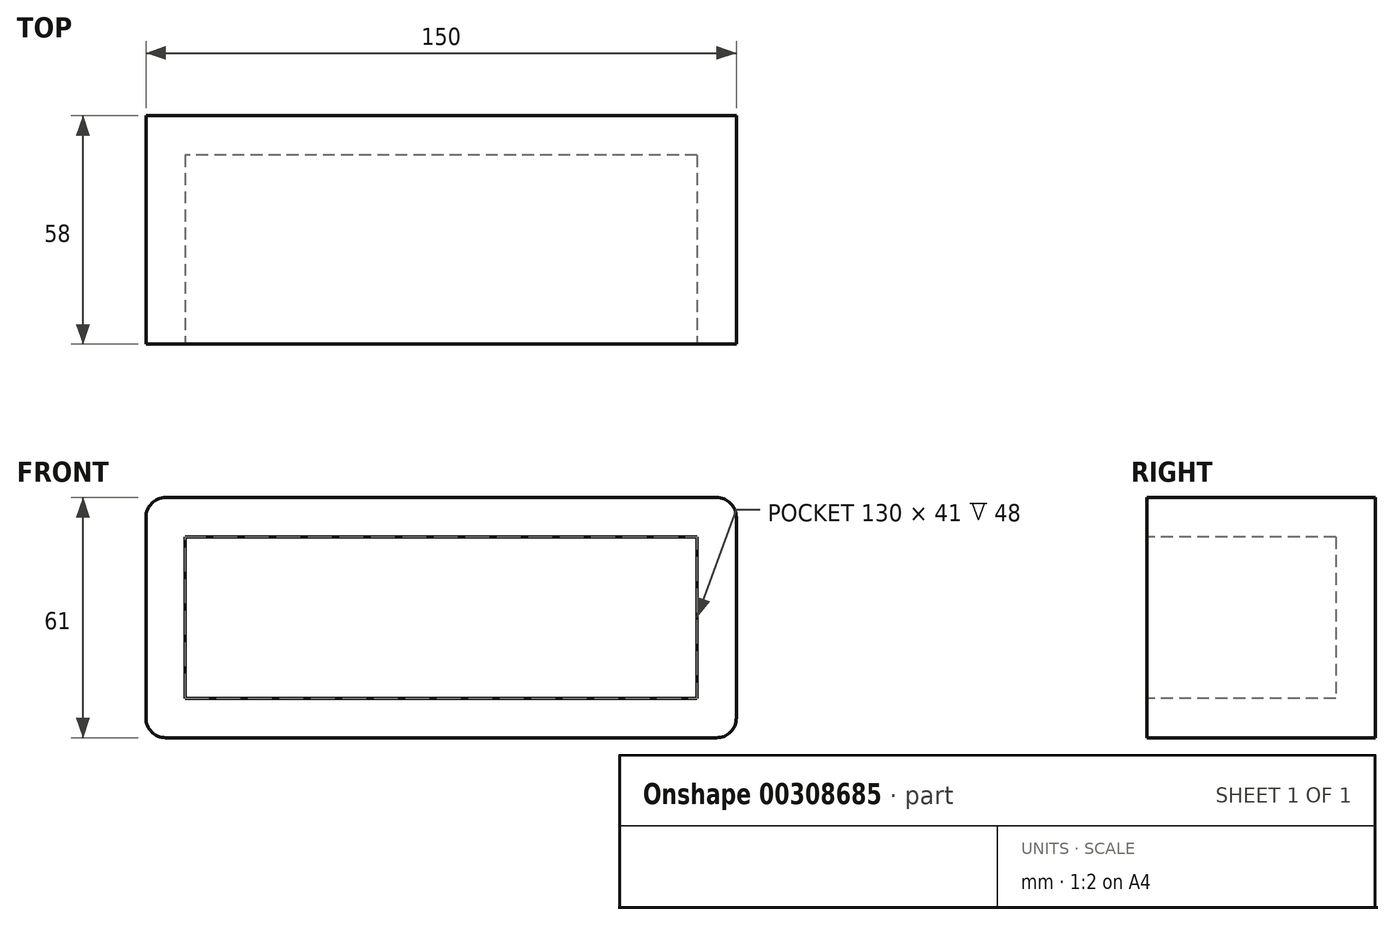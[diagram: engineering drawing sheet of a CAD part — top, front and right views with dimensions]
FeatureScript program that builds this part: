
annotation { "Feature Type Name" : "Feature", "Feature Type Description" : "" }
export const myFeature = defineFeature(function(context is Context, id is Id, definition is map)
    precondition{}
    {
        {
            var Q0;
            Q0=qCreatedBy(makeId("Front.planeOp"),FACE);
            var sketch = newSketch(context, id + "F0", { "sketchPlane" : qUnion([Q0])});
            skLineSegment(sketch, "E0.bottom", {"start": v(75, 29.55) * mm, "end": v(-75, 29.55) * mm});
            skLineSegment(sketch, "E0.top", {"start": v(75, -31.45) * mm, "end": v(-75, -31.45) * mm});
            skLineSegment(sketch, "E0.left", {"start": v(75, 29.55) * mm, "end": v(75, -31.45) * mm});
            skLineSegment(sketch, "E0.right", {"start": v(-75, 29.55) * mm, "end": v(-75, -31.45) * mm});
            skPoint(sketch, "E0.middle", {"position": v(0, -0.95) * mm});
            skSolve(sketch);
        }
        {
            var Q0;
            Q0 = qSketchRegion(id + "F0", true);
            extrude(context, id + "F1", {"entities" : qUnion([Q0]), "depth" : 58 * mm});
        }
        {
            var Q0;
            Q0=makeQuery(id+"F1.opExtrude","SWEPT_EDGE",EDGE,{"disambiguationData":[OSD([sQuery(id+"F0.wireOp",EDGE,"E0.bottom"),sQuery(id+"F0.wireOp",EDGE,"E0.right")])]});
            var Q1;
            Q1=makeQuery(id+"F1.opExtrude","SWEPT_EDGE",EDGE,{"disambiguationData":[OSD([sQuery(id+"F0.wireOp",EDGE,"E0.bottom"),sQuery(id+"F0.wireOp",EDGE,"E0.left")])]});
            var Q2;
            Q2=makeQuery(id+"F1.opExtrude","SWEPT_EDGE",EDGE,{"disambiguationData":[OSD([sQuery(id+"F0.wireOp",EDGE,"E0.top"),sQuery(id+"F0.wireOp",EDGE,"E0.left")])]});
            var Q3;
            Q3=makeQuery(id+"F1.opExtrude","SWEPT_EDGE",EDGE,{"disambiguationData":[OSD([sQuery(id+"F0.wireOp",EDGE,"E0.top"),sQuery(id+"F0.wireOp",EDGE,"E0.right")])]});
            fillet(context, id + "F2", {"entities" : qUnion([Q0, Q1, Q2, Q3]), "radius" : 5 * mm, "tangentPropagation" : true, "allowEdgeOverflow" : false});
        }
        {
            var Q0;
            Q0=makeQuery(id+"F1.opExtrude","CAP_FACE",FACE,{"disambiguationData":[OSD([sQuery(id+"F0.wireOp",EDGE,"E0.bottom"),sQuery(id+"F0.wireOp",EDGE,"E0.top"),sQuery(id+"F0.wireOp",EDGE,"E0.left"),sQuery(id+"F0.wireOp",EDGE,"E0.right")])],"isStart":false});
            shell(context, id + "F3", {"entities" : qUnion([Q0]), "thickness" : 10 * mm});
        }
    });
